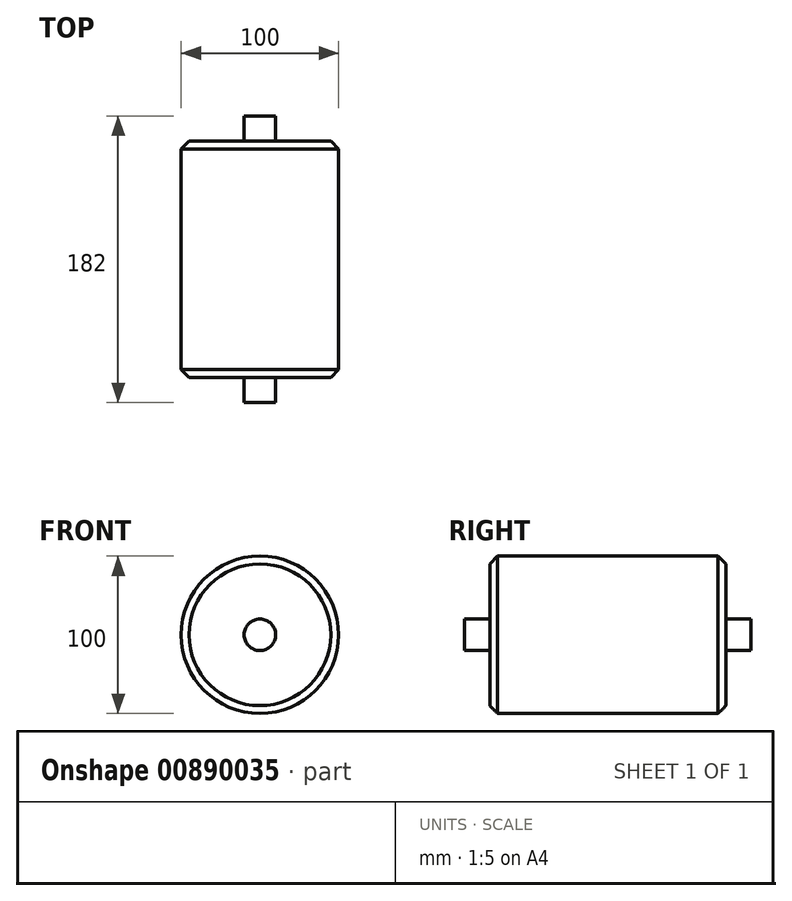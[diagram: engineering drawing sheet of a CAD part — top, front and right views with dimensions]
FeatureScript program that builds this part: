
annotation { "Feature Type Name" : "Feature", "Feature Type Description" : "" }
export const myFeature = defineFeature(function(context is Context, id is Id, definition is map)
    precondition{}
    {
        {
            var Q0;
            Q0=qCreatedBy(makeId("Front.planeOp"),FACE);
            var sketch = newSketch(context, id + "F0", { "sketchPlane" : qUnion([Q0])});
            skCircle(sketch, "E0", {"center": v(0, 0) * mm, "radius": 50 * mm});
            skSolve(sketch);
        }
        {
            var Q0;
            Q0 = qSketchRegion(id + "F0", true);
            extrude(context, id + "F1", {"entities" : qUnion([Q0]), "depth" : 75 * mm, "offsetDistance" : 25.4 * mm});
        }
        {
            var Q0;
            Q0=makeQuery(id+"F1.opExtrude","CAP_FACE",FACE,{"disambiguationData":[OSD([sQuery(id+"F0.wireOp",EDGE,"E0")])],"isStart":true});
            extrude(context, id + "F2", {"entities" : qUnion([Q0]), "operationType" : NewBodyOperationType.ADD, "depth" : 75 * mm, "offsetDistance" : 25.4 * mm});
        }
        {
            var Q0;
            Q0=makeQuery(id+"F1.opExtrude","CAP_FACE",FACE,{"disambiguationData":[OSD([sQuery(id+"F0.wireOp",EDGE,"E0")])],"isStart":false});
            var sketch = newSketch(context, id + "F3", { "sketchPlane" : qUnion([Q0])});
            skCircle(sketch, "E1", {"center": v(0, 0) * mm, "radius": 10 * mm});
            skSolve(sketch);
        }
        {
            var Q0;
            Q0 = qSketchRegion(id + "F3", true);
            extrude(context, id + "F4", {"entities" : qUnion([Q0]), "operationType" : NewBodyOperationType.ADD, "depth" : 16 * mm, "offsetDistance" : 25.4 * mm});
        }
        {
            var Q0;
            Q0=makeQuery(id+"F2.opExtrude","CAP_FACE",FACE,{"disambiguationData":[OSD([sQuery(id+"F0.wireOp",EDGE,"E0")])],"isStart":false});
            var sketch = newSketch(context, id + "F5", { "sketchPlane" : qUnion([Q0])});
            skCircle(sketch, "E2", {"center": v(0, 0) * mm, "radius": 10 * mm});
            skSolve(sketch);
        }
        {
            var Q0;
            Q0 = qSketchRegion(id + "F5", true);
            extrude(context, id + "F6", {"entities" : qUnion([Q0]), "operationType" : NewBodyOperationType.ADD, "depth" : 16 * mm, "offsetDistance" : 25.4 * mm});
        }
        {
            var Q0;
            Q0=makeQuery(id+"F2.opExtrude","CAP_EDGE",EDGE,{"disambiguationData":[OSD([sQuery(id+"F0.wireOp",EDGE,"E0")])],"isStart":false});
            chamfer(context, id + "F7", {"entities" : qUnion([Q0]), "width" : 5 * mm, "tangentPropagation" : true});
        }
        {
            var Q0;
            Q0=makeQuery(id+"F1.opExtrude","CAP_EDGE",EDGE,{"disambiguationData":[OSD([sQuery(id+"F0.wireOp",EDGE,"E0")])],"isStart":false});
            chamfer(context, id + "F8", {"entities" : qUnion([Q0]), "width" : 5 * mm, "tangentPropagation" : true});
        }
    });
